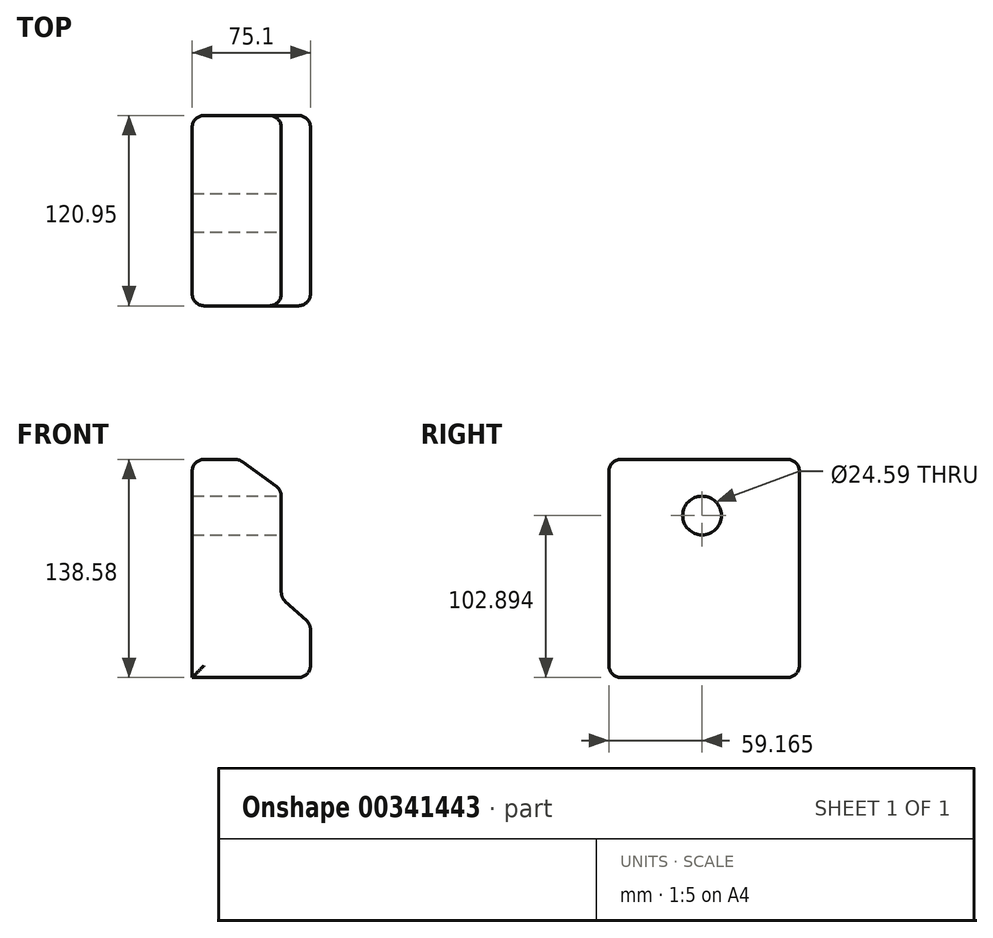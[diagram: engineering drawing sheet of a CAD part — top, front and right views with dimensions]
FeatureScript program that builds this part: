
annotation { "Feature Type Name" : "Feature", "Feature Type Description" : "" }
export const myFeature = defineFeature(function(context is Context, id is Id, definition is map)
    precondition{}
    {
        {
            var Q0;
            Q0=qCreatedBy(makeId("Front.planeOp"),FACE);
            var sketch = newSketch(context, id + "F0", { "sketchPlane" : qUnion([Q0])});
            skLineSegment(sketch, "E0", {"start": v(0, 60.16) * mm, "end": v(29.67, 60.16) * mm});
            skLineSegment(sketch, "E1", {"start": v(29.67, 60.16) * mm, "end": v(56.64, 40.66) * mm});
            skLineSegment(sketch, "E2", {"start": v(56.64, 40.66) * mm, "end": v(56.64, 0) * mm});
            skLineSegment(sketch, "E3", {"start": v(56.64, 0) * mm, "end": v(56.64, -27.8) * mm});
            skLineSegment(sketch, "E4", {"start": v(56.64, -27.8) * mm, "end": v(75.1, -44.4) * mm});
            skLineSegment(sketch, "E5", {"start": v(75.1, -44.4) * mm, "end": v(75.1, -78.42) * mm});
            skLineSegment(sketch, "E6", {"start": v(75.1, -78.42) * mm, "end": v(0, -78.42) * mm});
            skLineSegment(sketch, "E7", {"start": v(0, -78.42) * mm, "end": v(0, 60.16) * mm});
            skSolve(sketch);
        }
        {
            var Q0;
            Q0=makeQuery(id+"F0.imprint","IMPRINT",FACE,{"disambiguationData":[TD([[makeQuery(id+"F0.imprint","IMPRINT",EDGE,{"derivedFrom":sQuery(id+"F0.wireOp",EDGE,"E0")}),-1.0]])]});
            extrude(context, id + "F1", {"entities" : qUnion([Q0]), "depth" : 120.95 * mm});
        }
        {
            var Q0;
            Q0=makeQuery(id+"F1.opExtrude","SWEPT_EDGE",EDGE,{"disambiguationData":[OSD([sQuery(id+"F0.wireOp",EDGE,"E5"),sQuery(id+"F0.wireOp",EDGE,"E6")])]});
            var Q1;
            Q1=makeQuery(id+"F1.opExtrude","SWEPT_EDGE",EDGE,{"disambiguationData":[OSD([sQuery(id+"F0.wireOp",EDGE,"E4"),sQuery(id+"F0.wireOp",EDGE,"E5")])]});
            var Q2;
            Q2=makeQuery(id+"F1.opExtrude","SWEPT_EDGE",EDGE,{"disambiguationData":[OSD([sQuery(id+"F0.wireOp",EDGE,"E3"),sQuery(id+"F0.wireOp",EDGE,"E4")])]});
            var Q3;
            Q3=makeQuery(id+"F1.opExtrude","SWEPT_EDGE",EDGE,{"disambiguationData":[OSD([sQuery(id+"F0.wireOp",EDGE,"E1"),sQuery(id+"F0.wireOp",EDGE,"E2")])]});
            var Q4;
            Q4=makeQuery(id+"F1.opExtrude","SWEPT_FACE",FACE,{"disambiguationData":[OSD([sQuery(id+"F0.wireOp",EDGE,"E0")])]});
            var Q5;
            Q5=makeQuery(id+"F1.opExtrude","CAP_FACE",FACE,{"disambiguationData":[OSD([sQuery(id+"F0.wireOp",EDGE,"E0"),sQuery(id+"F0.wireOp",EDGE,"E1"),sQuery(id+"F0.wireOp",EDGE,"E2"),sQuery(id+"F0.wireOp",EDGE,"E3"),sQuery(id+"F0.wireOp",EDGE,"E4"),sQuery(id+"F0.wireOp",EDGE,"E5"),sQuery(id+"F0.wireOp",EDGE,"E6"),sQuery(id+"F0.wireOp",EDGE,"E7")])],"isStart":false});
            var Q6;
            Q6=makeQuery(id+"F1.opExtrude","CAP_FACE",FACE,{"disambiguationData":[OSD([sQuery(id+"F0.wireOp",EDGE,"E0"),sQuery(id+"F0.wireOp",EDGE,"E1"),sQuery(id+"F0.wireOp",EDGE,"E2"),sQuery(id+"F0.wireOp",EDGE,"E3"),sQuery(id+"F0.wireOp",EDGE,"E4"),sQuery(id+"F0.wireOp",EDGE,"E5"),sQuery(id+"F0.wireOp",EDGE,"E6"),sQuery(id+"F0.wireOp",EDGE,"E7")])],"isStart":true});
            fillet(context, id + "F2", {"entities" : qUnion([Q0, Q1, Q2, Q3, Q4, Q5, Q6]), "radius" : 7.62 * mm, "tangentPropagation" : true, "allowEdgeOverflow" : false});
        }
        {
            var Q0;
            Q0=makeQuery(id+"F1.opExtrude","SWEPT_FACE",FACE,{"disambiguationData":[OSD([sQuery(id+"F0.wireOp",EDGE,"E2"),sQuery(id+"F0.wireOp",EDGE,"E3")])]});
            var sketch = newSketch(context, id + "F3", { "sketchPlane" : qUnion([Q0])});
            skCircle(sketch, "E8", {"center": v(-61.79, 24.47) * mm, "radius": 12.3 * mm});
            skSolve(sketch);
        }
        {
            var Q0;
            Q0=makeQuery(id+"F3.imprint","IMPRINT",FACE,{"disambiguationData":[TD([[makeQuery(id+"F3.imprint","IMPRINT",EDGE,{"derivedFrom":sQuery(id+"F3.wireOp",EDGE,"E8")}),1.0]])]});
            extrude(context, id + "F4", {"entities" : qUnion([Q0]), "operationType" : NewBodyOperationType.REMOVE, "oppositeDirection" : true, "depth" : 191.02 * mm});
        }
    });
